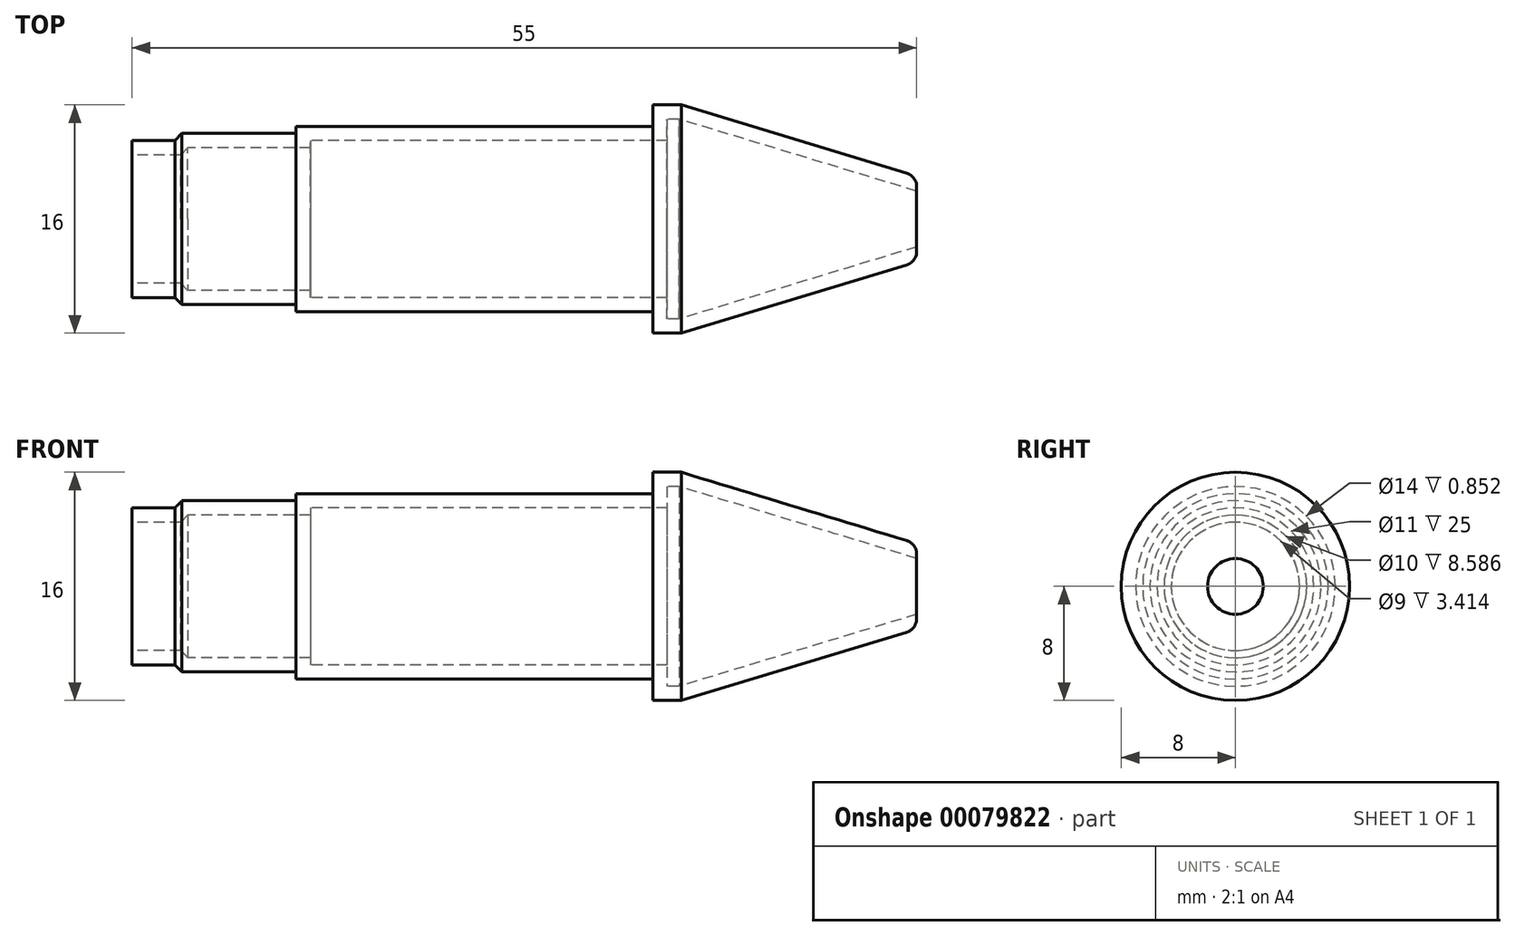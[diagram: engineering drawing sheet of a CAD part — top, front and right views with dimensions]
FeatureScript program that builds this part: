
annotation { "Feature Type Name" : "Feature", "Feature Type Description" : "" }
export const myFeature = defineFeature(function(context is Context, id is Id, definition is map)
    precondition{}
    {
        {
            var Q0;
            Q0=qCreatedBy(makeId("Front.planeOp"),FACE);
            var sketch = newSketch(context, id + "F0", { "sketchPlane" : qUnion([Q0])});
            skLineSegment(sketch, "E0", {"start": v(0, 0) * mm, "end": v(55, 0) * mm});
            skLineSegment(sketch, "E1", {"start": v(0, 0) * mm, "end": v(0, 5.5) * mm});
            skLineSegment(sketch, "E2", {"start": v(0, 5.5) * mm, "end": v(3, 5.5) * mm});
            skLineSegment(sketch, "E3", {"start": v(3, 5.5) * mm, "end": v(3.5, 6) * mm});
            skLineSegment(sketch, "E4", {"start": v(3.5, 6) * mm, "end": v(11.5, 6) * mm});
            skLineSegment(sketch, "E5", {"start": v(11.5, 6) * mm, "end": v(11.5, 6.5) * mm});
            skLineSegment(sketch, "E6", {"start": v(11.5, 6.5) * mm, "end": v(36.5, 6.5) * mm});
            skLineSegment(sketch, "E7", {"start": v(36.5, 6.5) * mm, "end": v(36.5, 8) * mm});
            skLineSegment(sketch, "E8", {"start": v(36.5, 8) * mm, "end": v(38.5, 8) * mm});
            skLineSegment(sketch, "E9", {"start": v(55, 0) * mm, "end": v(55, 3) * mm});
            skLineSegment(sketch, "E10", {"start": v(38.5, 8) * mm, "end": v(55, 3) * mm});
            skSolve(sketch);
        }
        {
            var Q0;
            Q0=qCreatedBy(makeId("Front.planeOp"),FACE);
            var sketch = newSketch(context, id + "F1", { "sketchPlane" : qUnion([Q0])});
            skLineSegment(sketch, "E11", {"start": v(-56.36, 0) * mm, "end": v(67.18, 0) * mm});
            skSolve(sketch);
        }
        {
            var Q0;
            Q0 = qSketchRegion(id + "F0", true);
            var Q1;
            Q1 = qBodyType(qCreatedBy(id + "F1" ,EDGE), BodyType.WIRE);
            revolve(context, id + "F4", {"entities" : qUnion([Q0]), "axis" : qUnion([Q1]), "revolveType" : RevolveType.FULL});
        }
        {
            var Q0;
            Q0=makeQuery(id+"F4.opRevolve","SWEPT_FACE",FACE,{"disambiguationData":[OSD([sQuery(id+"F0.wireOp",EDGE,"E1")])]});
            var Q1;
            Q1=makeQuery(id+"F4.opRevolve","SWEPT_FACE",FACE,{"disambiguationData":[OSD([sQuery(id+"F0.wireOp",EDGE,"E9")])]});
            shell(context, id + "F2", {"entities" : qUnion([Q0, Q1]), "thickness" : 1 * mm});
        }
        {
            var Q0;
            Q0=makeQuery(id+"F4.opRevolve","SWEPT_EDGE",EDGE,{"disambiguationData":[OSD([sQuery(id+"F0.wireOp",EDGE,"E9"),sQuery(id+"F0.wireOp",EDGE,"E10")])]});
            fillet(context, id + "F3", {"entities" : qUnion([Q0]), "radius" : 1 * mm, "tangentPropagation" : true, "allowEdgeOverflow" : false});
        }
    });
